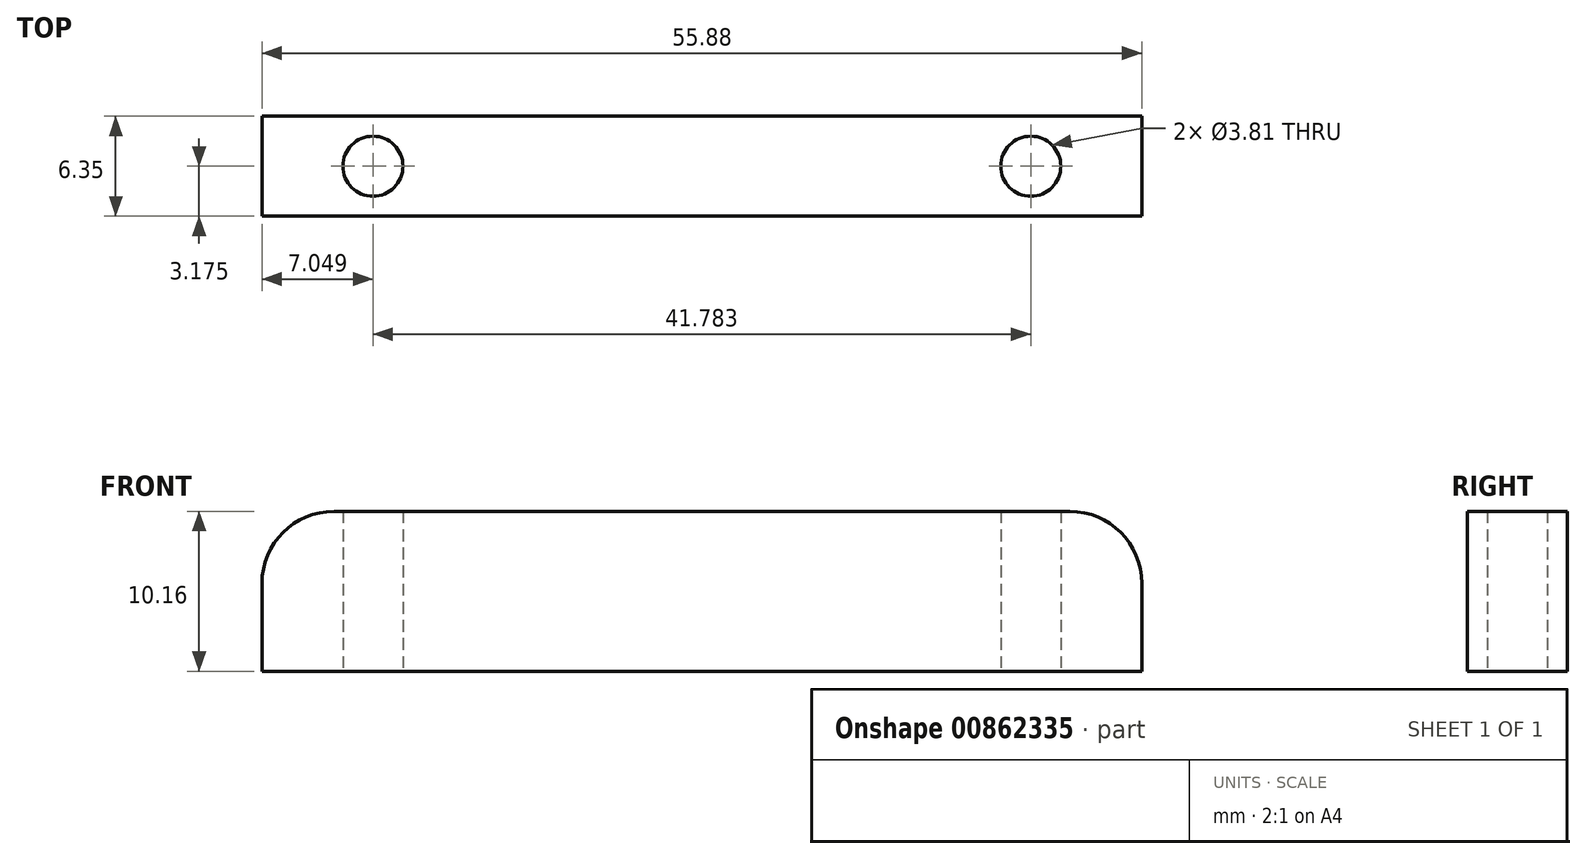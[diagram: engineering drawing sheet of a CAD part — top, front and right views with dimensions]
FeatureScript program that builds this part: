
annotation { "Feature Type Name" : "Feature", "Feature Type Description" : "" }
export const myFeature = defineFeature(function(context is Context, id is Id, definition is map)
    precondition{}
    {
        {
            var Q0;
            Q0=qCreatedBy(makeId("Front.planeOp"),FACE);
            var sketch = newSketch(context, id + "F0", { "sketchPlane" : qUnion([Q0])});
            skLineSegment(sketch, "E0.bottom", {"start": v(23.37, 5.08) * mm, "end": v(-23.37, 5.08) * mm});
            skLineSegment(sketch, "E0.top", {"start": v(27.94, -5.08) * mm, "end": v(-27.94, -5.08) * mm});
            skLineSegment(sketch, "E0.left", {"start": v(27.94, 0.5) * mm, "end": v(27.94, -5.08) * mm});
            skLineSegment(sketch, "E0.right", {"start": v(-27.94, 0.5) * mm, "end": v(-27.94, -5.08) * mm});
            skPoint(sketch, "E0.middle", {"position": v(0, 0) * mm});
            skPoint(sketch, "E1.visualSharp", {"position": v(-27.94, 5.08) * mm});
            skArc(sketch, "E1.filletArc", {"start": v(-23.37, 5.08) * mm, "mid": v(-26.6, 3.74) * mm, "end": v(-27.94, 0.5) * mm});
            skPoint(sketch, "E2.visualSharp", {"position": v(27.94, 5.08) * mm});
            skArc(sketch, "E2.filletArc", {"start": v(27.94, 0.5) * mm, "mid": v(26.6, 3.74) * mm, "end": v(23.37, 5.08) * mm});
            skSolve(sketch);
        }
        {
            var Q0;
            Q0 = qSketchRegion(id + "F0", true);
            extrude(context, id + "F1", {"entities" : qUnion([Q0]), "depth" : 6.35 * mm, "offsetDistance" : 25.4 * mm});
        }
        {
            var Q0;
            Q0=makeQuery(id+"F1.opExtrude","SWEPT_FACE",FACE,{"disambiguationData":[OSD([sQuery(id+"F0.wireOp",EDGE,"E0.top")])]});
            var sketch = newSketch(context, id + "F2", { "sketchPlane" : qUnion([Q0])});
            skLineSegment(sketch, "E3", {"start": v(0, 6.35) * mm, "end": v(0, 0) * mm, "construction": true});
            skLineSegment(sketch, "E4", {"start": v(0, 3.18) * mm, "end": v(20.9, 3.18) * mm, "construction": true});
            skCircle(sketch, "E5", {"center": v(20.9, 3.18) * mm, "radius": 1.9 * mm});
            skCircle(sketch, "E6.MirrorC", {"center": v(-20.9, 3.17) * mm, "radius": 1.9 * mm});
            skSolve(sketch);
        }
        {
            var Q0;
            Q0 = qSketchRegion(id + "F2", true);
            extrude(context, id + "F3", {"entities" : qUnion([Q0]), "operationType" : NewBodyOperationType.REMOVE, "oppositeDirection" : true, "depth" : 25.4 * mm, "offsetDistance" : 25.4 * mm});
        }
    });
